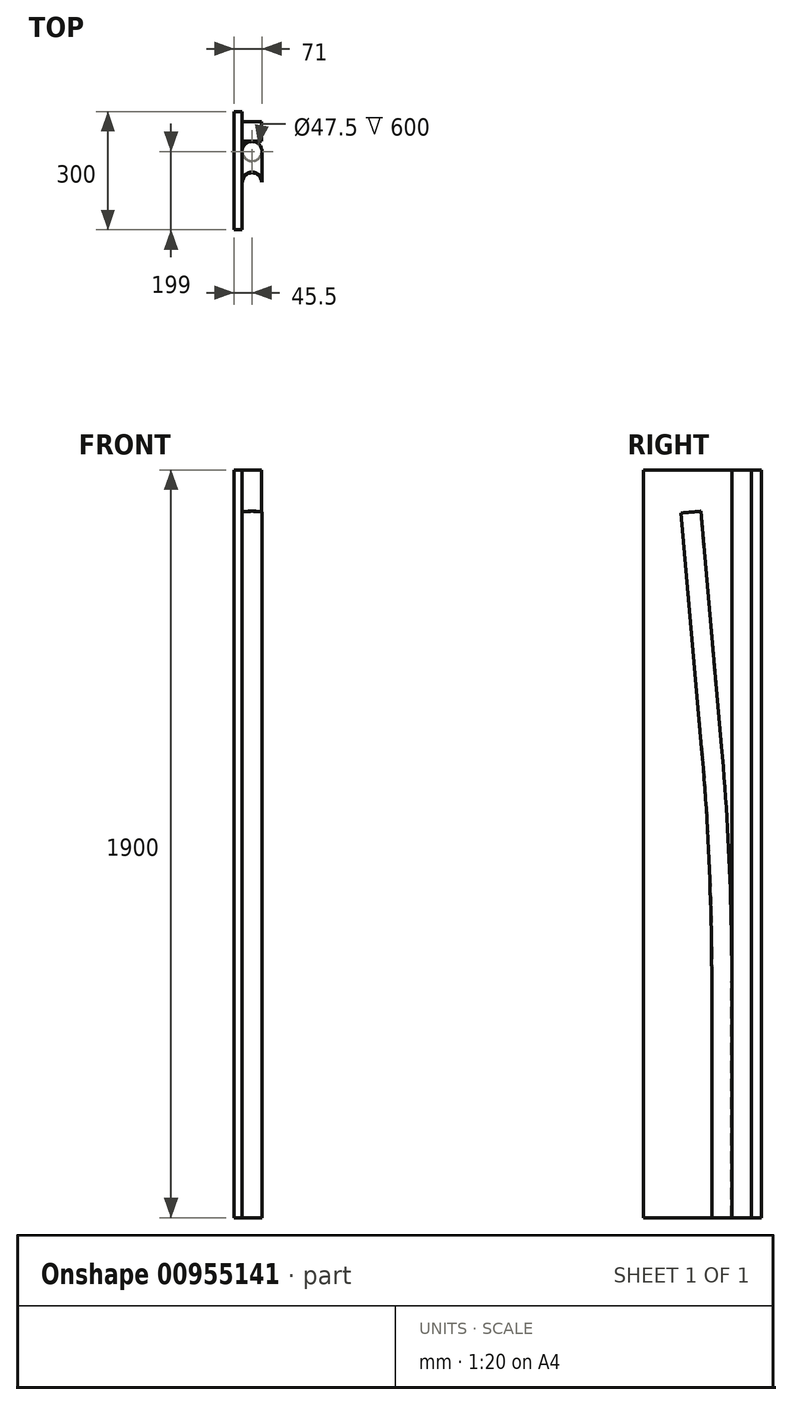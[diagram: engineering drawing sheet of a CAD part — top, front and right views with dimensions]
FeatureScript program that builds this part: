
annotation { "Feature Type Name" : "Feature", "Feature Type Description" : "" }
export const myFeature = defineFeature(function(context is Context, id is Id, definition is map)
    precondition{}
    {
        {
            var Q0;
            Q0=qCreatedBy(makeId("Top.planeOp"),FACE);
            var sketch = newSketch(context, id + "F0", { "sketchPlane" : qUnion([Q0])});
            skCircle(sketch, "E0", {"center": v(0, 0) * mm, "radius": 25.5 * mm});
            skCircle(sketch, "E1", {"center": v(0, 0) * mm, "radius": 23.75 * mm});
            skSolve(sketch);
        }
        {
            var Q0;
            Q0=qCreatedBy(makeId("Right.planeOp"),FACE);
            var sketch = newSketch(context, id + "F1", { "sketchPlane" : qUnion([Q0])});
            skLineSegment(sketch, "E2", {"start": v(0, 0) * mm, "end": v(0, 898) * mm, "construction": true});
            skLineSegment(sketch, "E3", {"start": v(0, 898) * mm, "end": v(-77.9, 1792.61) * mm, "construction": true});
            skPoint(sketch, "E4", {"position": v(0, 600) * mm});
            skLineSegment(sketch, "E5", {"start": v(0, 600) * mm, "end": v(0, 600) * mm});
            skPoint(sketch, "E6", {"position": v(-25.85, 1194.88) * mm});
            skLineSegment(sketch, "E7", {"start": v(-25.85, 1194.88) * mm, "end": v(-6857.5, 600) * mm, "construction": true});
            skPoint(sketch, "E8", {"position": v(-6857.5, 600) * mm});
            skArc(sketch, "E9", {"start": v(0, 600) * mm, "mid": v(-6.47, 897.72) * mm, "end": v(-25.85, 1194.88) * mm});
            skLineSegment(sketch, "E10", {"start": v(0, 0) * mm, "end": v(0, 600) * mm});
            skLineSegment(sketch, "E11", {"start": v(0, 600) * mm, "end": v(-6857.5, 600) * mm, "construction": true});
            skLineSegment(sketch, "E12", {"start": v(-77.9, 1792.61) * mm, "end": v(-25.85, 1194.88) * mm, "construction": true});
            skLineSegment(sketch, "E13", {"start": v(-25.85, 1194.88) * mm, "end": v(-77.9, 1792.61) * mm});
            skPoint(sketch, "E14", {"position": v(-8.19, 935) * mm});
            skLineSegment(sketch, "E15", {"start": v(0, 898) * mm, "end": v(0, 996.23) * mm, "construction": true});
            skSolve(sketch);
        }
        {
            var Q0;
            Q0=makeQuery(id+"F0.imprint","IMPRINT",FACE,{"disambiguationData":[TD([[makeQuery(id+"F0.imprint","IMPRINT",EDGE,{"derivedFrom":sQuery(id+"F0.wireOp",EDGE,"E0")}),1.0]])]});
            var Q1;
            Q1=sQuery(id+"F1.wireOp",EDGE,"E10");
            var Q2;
            Q2=sQuery(id+"F1.wireOp",EDGE,"E9");
            var Q3;
            Q3=sQuery(id+"F1.wireOp",EDGE,"E13");
            sweep(context, id + "F2", {"profiles" : qUnion([Q0]), "path" : qUnion([Q1, Q2, Q3])});
        }
        {
            var Q0;
            Q0=qCreatedBy(makeId("Top.planeOp"),FACE);
            var Q1;
            Q1=qCreatedBy(makeId("Top.planeOp"),FACE);
            var sketch = newSketch(context, id + "F3", { "sketchPlane" : qUnion([Q0, Q1])});
            skLineSegment(sketch, "E16", {"start": v(-25.5, 101) * mm, "end": v(-25.5, -199) * mm});
            skLineSegment(sketch, "E17", {"start": v(-25.5, -199) * mm, "end": v(-45.5, -199) * mm});
            skLineSegment(sketch, "E18", {"start": v(-45.5, -199) * mm, "end": v(-45.5, 101) * mm});
            skLineSegment(sketch, "E19", {"start": v(-45.5, 101) * mm, "end": v(-25.5, 101) * mm});
            skSolve(sketch);
        }
        {
            var Q0;
            Q0 = qSketchRegion(id + "F3", true);
            extrude(context, id + "F4", {"entities" : qUnion([Q0]), "operationType" : NewBodyOperationType.ADD, "depth" : 1900 * mm, "offsetDistance" : 25 * mm});
        }
        {
            var Q0;
            Q0=qCreatedBy(makeId("Top.planeOp"),FACE);
            var sketch = newSketch(context, id + "F5", { "sketchPlane" : qUnion([Q0])});
            skSolve(sketch);
        }
        {
            var Q0;
            Q0=qCreatedBy(makeId("Top.planeOp"),FACE);
            var sketch = newSketch(context, id + "F6", { "sketchPlane" : qUnion([Q0])});
            skLineSegment(sketch, "E20", {"start": v(0, 25.5) * mm, "end": v(24.5, 25.5) * mm});
            skLineSegment(sketch, "E21", {"start": v(24.5, 25.5) * mm, "end": v(24.5, 75.5) * mm});
            skLineSegment(sketch, "E22", {"start": v(24.5, 75.5) * mm, "end": v(-25.5, 75.5) * mm});
            skLineSegment(sketch, "E23", {"start": v(-25.5, 75.5) * mm, "end": v(-25.5, 25.5) * mm});
            skLineSegment(sketch, "E24", {"start": v(-25.5, 25.5) * mm, "end": v(0, 25.5) * mm});
            skSolve(sketch);
        }
        {
            var Q0;
            Q0 = qSketchRegion(id + "F5", true);
            var Q1;
            Q1=makeQuery(id+"F6.imprint","IMPRINT",FACE,{"disambiguationData":[TD([[makeQuery(id+"F6.imprint","IMPRINT",EDGE,{"derivedFrom":sQuery(id+"F6.wireOp",EDGE,"E20")}),1.0]])]});
            extrude(context, id + "F7", {"entities" : qUnion([Q0, Q1]), "depth" : 1900 * mm, "offsetDistance" : 25 * mm});
        }
    });
